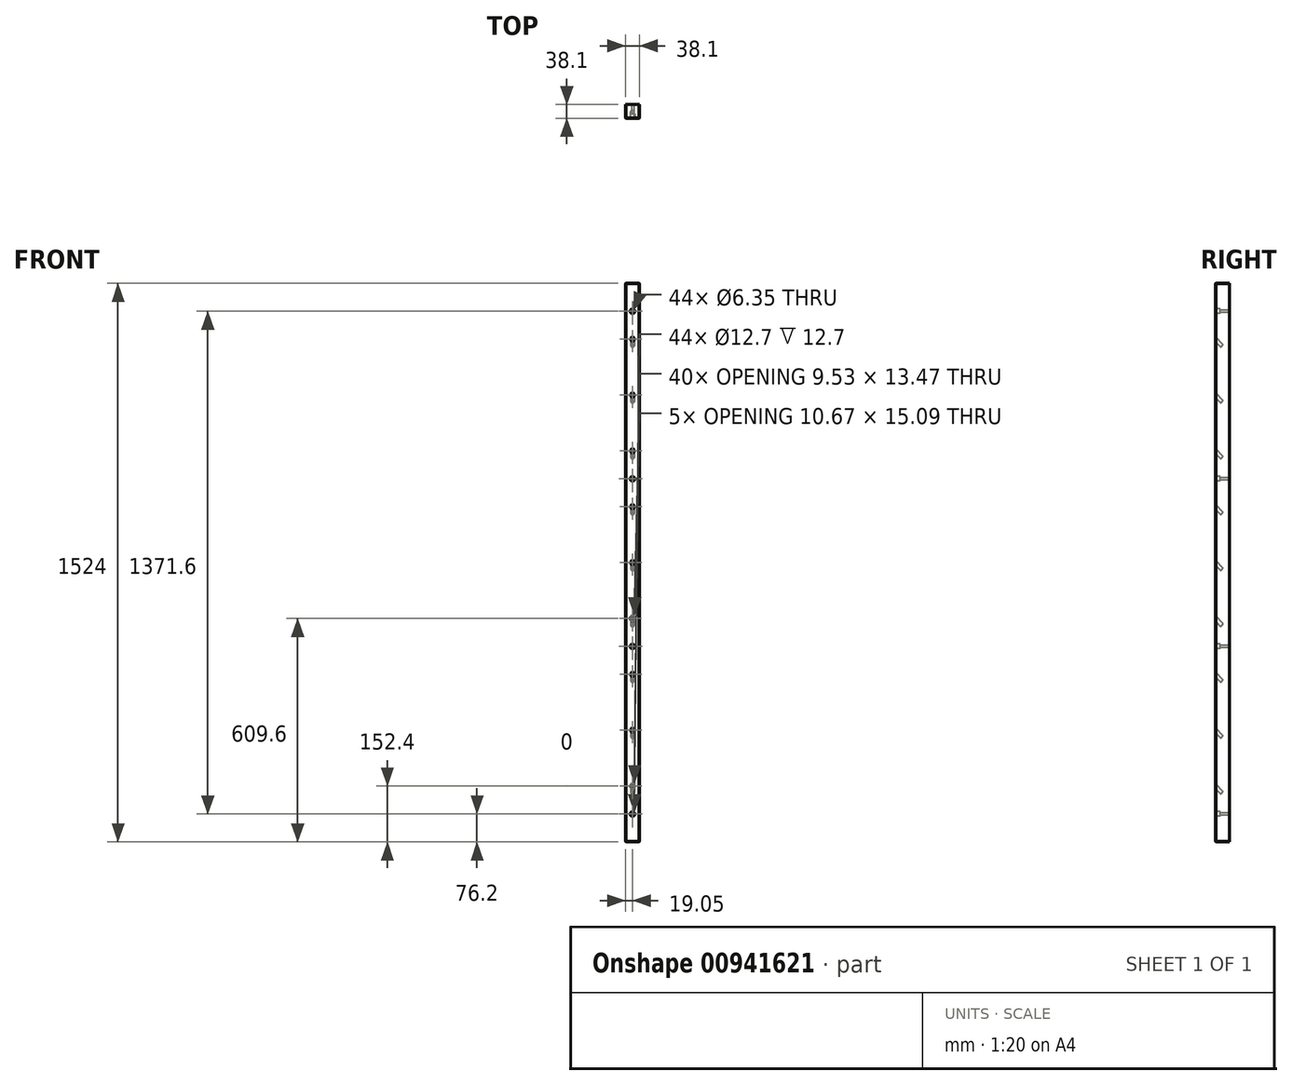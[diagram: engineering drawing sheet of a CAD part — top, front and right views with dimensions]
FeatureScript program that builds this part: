
annotation { "Feature Type Name" : "Feature", "Feature Type Description" : "" }
export const myFeature = defineFeature(function(context is Context, id is Id, definition is map)
    precondition{}
    {
        {
            var Q0;
            Q0=qCreatedBy(makeId("Front.planeOp"),FACE);
            var sketch = newSketch(context, id + "F0", { "sketchPlane" : qUnion([Q0])});
            skLineSegment(sketch, "E0.bottom", {"start": v(19.05, -762) * mm, "end": v(-19.05, -762) * mm});
            skLineSegment(sketch, "E0.top", {"start": v(19.05, 762) * mm, "end": v(-19.05, 762) * mm});
            skLineSegment(sketch, "E0.left", {"start": v(19.05, -762) * mm, "end": v(19.05, 762) * mm});
            skLineSegment(sketch, "E0.right", {"start": v(-19.05, -762) * mm, "end": v(-19.05, 762) * mm});
            skPoint(sketch, "E0.middle", {"position": v(0, 0) * mm});
            skSolve(sketch);
        }
        {
            var Q0;
            Q0=makeQuery(id+"F0.imprint","IMPRINT",FACE,{"disambiguationData":[TD([[makeQuery(id+"F0.imprint","IMPRINT",EDGE,{"derivedFrom":sQuery(id+"F0.wireOp",EDGE,"E0.bottom")}),-1.0]])]});
            extrude(context, id + "F1", {"entities" : qUnion([Q0]), "depth" : 38.1 * mm, "offsetDistance" : 25.4 * mm});
        }
        {
            var Q0;
            Q0=makeQuery(id+"F1.opExtrude","CAP_FACE",FACE,{"disambiguationData":[OSD([sQuery(id+"F0.wireOp",EDGE,"E0.bottom"),sQuery(id+"F0.wireOp",EDGE,"E0.top"),sQuery(id+"F0.wireOp",EDGE,"E0.left"),sQuery(id+"F0.wireOp",EDGE,"E0.right")])],"isStart":false});
            var sketch = newSketch(context, id + "F2", { "sketchPlane" : qUnion([Q0])});
            skPoint(sketch, "E1", {"position": v(0, 609.6) * mm});
            skPoint(sketch, "E1.positionSnap0", {"position": v(0, 762) * mm});
            skPoint(sketch, "E2", {"position": v(0, 457.2) * mm});
            skPoint(sketch, "E3", {"position": v(0, 304.8) * mm});
            skPoint(sketch, "E4", {"position": v(0, 152.4) * mm});
            skPoint(sketch, "E5", {"position": v(0, 0) * mm});
            skPoint(sketch, "E6", {"position": v(0, -152.4) * mm});
            skPoint(sketch, "E7", {"position": v(0, -304.8) * mm});
            skPoint(sketch, "E8", {"position": v(0, -457.2) * mm});
            skPoint(sketch, "E9", {"position": v(0, -609.6) * mm});
            skLineSegment(sketch, "E10", {"start": v(-19.05, 609.6) * mm, "end": v(19.05, 609.6) * mm});
            skLineSegment(sketch, "E11", {"start": v(-19.05, 457.2) * mm, "end": v(19.05, 457.2) * mm});
            skLineSegment(sketch, "E12", {"start": v(-19.05, 304.8) * mm, "end": v(19.05, 304.8) * mm});
            skLineSegment(sketch, "E13", {"start": v(-19.05, 152.4) * mm, "end": v(19.05, 152.4) * mm});
            skLineSegment(sketch, "E14", {"start": v(-19.05, -152.4) * mm, "end": v(19.05, -152.4) * mm});
            skLineSegment(sketch, "E15", {"start": v(-19.05, -304.8) * mm, "end": v(19.05, -304.8) * mm});
            skLineSegment(sketch, "E16", {"start": v(-19.05, -457.2) * mm, "end": v(19.05, -457.2) * mm});
            skLineSegment(sketch, "E17", {"start": v(-19.05, -609.6) * mm, "end": v(19.05, -609.6) * mm});
            skLineSegment(sketch, "E18", {"start": v(-19.05, 0) * mm, "end": v(19.05, 0) * mm});
            skPoint(sketch, "E19", {"position": v(0, 685.8) * mm});
            skPoint(sketch, "E20", {"position": v(0, 228.6) * mm});
            skPoint(sketch, "E21", {"position": v(0, -228.6) * mm});
            skPoint(sketch, "E22", {"position": v(0, -685.8) * mm});
            skSolve(sketch);
        }
        {
            var Q0;
            Q0=sQuery(id+"F2.wireOp",EDGE,"E10");
            cPlane(context, id + "F3", {"entities" : qUnion([Q0]), "cplaneType" : CPlaneType.LINE_ANGLE, "offset" : 25.4 * mm, "angle" : 135 * degree, "width" : 152.4 * mm, "height" : 152.4 * mm});
        }
        {
            var Q0;
            Q0=qCreatedBy(id+"F3.planeOp",FACE);
            var sketch = newSketch(context, id + "F4", { "sketchPlane" : qUnion([Q0])});
            skCircle(sketch, "E23", {"center": v(0, 404.11) * mm, "radius": 4.76 * mm});
            skSolve(sketch);
        }
        {
            var Q0;
            Q0=sQuery(id+"F2.wireOp",EDGE,"E11");
            cPlane(context, id + "F5", {"entities" : qUnion([Q0]), "cplaneType" : CPlaneType.LINE_ANGLE, "offset" : 25.4 * mm, "angle" : 135 * degree, "width" : 152.4 * mm, "height" : 152.4 * mm});
        }
        {
            var Q0;
            Q0=qCreatedBy(id+"F5.planeOp",FACE);
            var sketch = newSketch(context, id + "F6", { "sketchPlane" : qUnion([Q0])});
            skCircle(sketch, "E24", {"center": v(0, 296.35) * mm, "radius": 4.76 * mm});
            skSolve(sketch);
        }
        {
            var Q0;
            Q0=sQuery(id+"F2.wireOp",EDGE,"E12");
            cPlane(context, id + "F7", {"entities" : qUnion([Q0]), "cplaneType" : CPlaneType.LINE_ANGLE, "offset" : 25.4 * mm, "angle" : 135 * degree, "width" : 152.4 * mm, "height" : 152.4 * mm});
        }
        {
            var Q0;
            Q0=qCreatedBy(id+"F7.planeOp",FACE);
            var sketch = newSketch(context, id + "F8", { "sketchPlane" : qUnion([Q0])});
            skCircle(sketch, "E25", {"center": v(0, 188.59) * mm, "radius": 4.76 * mm});
            skSolve(sketch);
        }
        {
            var Q0;
            Q0=sQuery(id+"F2.wireOp",EDGE,"E13");
            cPlane(context, id + "F9", {"entities" : qUnion([Q0]), "cplaneType" : CPlaneType.LINE_ANGLE, "offset" : 25.4 * mm, "angle" : 135 * degree, "width" : 152.4 * mm, "height" : 152.4 * mm});
        }
        {
            var Q0;
            Q0=qCreatedBy(id+"F9.planeOp",FACE);
            var sketch = newSketch(context, id + "F10", { "sketchPlane" : qUnion([Q0])});
            skCircle(sketch, "E26", {"center": v(0, 80.82) * mm, "radius": 4.76 * mm});
            skSolve(sketch);
        }
        {
            var Q0;
            Q0=sQuery(id+"F2.wireOp",EDGE,"E18");
            cPlane(context, id + "F11", {"entities" : qUnion([Q0]), "cplaneType" : CPlaneType.LINE_ANGLE, "offset" : 25.4 * mm, "angle" : 135 * degree, "width" : 152.4 * mm, "height" : 152.4 * mm});
        }
        {
            var Q0;
            Q0=qCreatedBy(id+"F11.planeOp",FACE);
            var sketch = newSketch(context, id + "F12", { "sketchPlane" : qUnion([Q0])});
            skCircle(sketch, "E27", {"center": v(0, -26.94) * mm, "radius": 4.76 * mm});
            skSolve(sketch);
        }
        {
            var Q0;
            Q0=sQuery(id+"F2.wireOp",EDGE,"E14");
            cPlane(context, id + "F13", {"entities" : qUnion([Q0]), "cplaneType" : CPlaneType.LINE_ANGLE, "offset" : 25.4 * mm, "angle" : 135 * degree, "width" : 152.4 * mm, "height" : 152.4 * mm});
        }
        {
            var Q0;
            Q0=qCreatedBy(id+"F13.planeOp",FACE);
            var sketch = newSketch(context, id + "F14", { "sketchPlane" : qUnion([Q0])});
            skCircle(sketch, "E28", {"center": v(0, -134.7) * mm, "radius": 5.34 * mm});
            skSolve(sketch);
        }
        {
            var Q0;
            Q0=sQuery(id+"F2.wireOp",EDGE,"E15");
            cPlane(context, id + "F15", {"entities" : qUnion([Q0]), "cplaneType" : CPlaneType.LINE_ANGLE, "offset" : 25.4 * mm, "angle" : 135 * degree, "width" : 152.4 * mm, "height" : 152.4 * mm});
        }
        {
            var Q0;
            Q0=qCreatedBy(id+"F15.planeOp",FACE);
            var sketch = newSketch(context, id + "F16", { "sketchPlane" : qUnion([Q0])});
            skCircle(sketch, "E29", {"center": v(0, -242.47) * mm, "radius": 4.76 * mm});
            skSolve(sketch);
        }
        {
            var Q0;
            Q0=sQuery(id+"F2.wireOp",EDGE,"E16");
            cPlane(context, id + "F17", {"entities" : qUnion([Q0]), "cplaneType" : CPlaneType.LINE_ANGLE, "offset" : 25.4 * mm, "angle" : 135 * degree, "width" : 152.4 * mm, "height" : 152.4 * mm});
        }
        {
            var Q0;
            Q0=qCreatedBy(id+"F17.planeOp",FACE);
            var sketch = newSketch(context, id + "F18", { "sketchPlane" : qUnion([Q0])});
            skCircle(sketch, "E30", {"center": v(0, -350.23) * mm, "radius": 4.76 * mm});
            skSolve(sketch);
        }
        {
            var Q0;
            Q0=sQuery(id+"F2.wireOp",EDGE,"E17");
            cPlane(context, id + "F19", {"entities" : qUnion([Q0]), "cplaneType" : CPlaneType.LINE_ANGLE, "offset" : 25.4 * mm, "angle" : 135 * degree, "width" : 152.4 * mm, "height" : 152.4 * mm});
        }
        {
            var Q0;
            Q0=qCreatedBy(id+"F19.planeOp",FACE);
            var sketch = newSketch(context, id + "F20", { "sketchPlane" : qUnion([Q0])});
            skCircle(sketch, "E31", {"center": v(0, -458) * mm, "radius": 4.76 * mm});
            skSolve(sketch);
        }
        {
            var Q0;
            Q0=makeQuery(id+"F4.imprint","IMPRINT",FACE,{"disambiguationData":[TD([[makeQuery(id+"F4.imprint","IMPRINT",EDGE,{"derivedFrom":sQuery(id+"F4.wireOp",EDGE,"E23")}),1.0]])]});
            var Q1;
            Q1=makeQuery(id+"F6.imprint","IMPRINT",FACE,{"disambiguationData":[TD([[makeQuery(id+"F6.imprint","IMPRINT",EDGE,{"derivedFrom":sQuery(id+"F6.wireOp",EDGE,"E24")}),1.0]])]});
            var Q2;
            Q2=makeQuery(id+"F8.imprint","IMPRINT",FACE,{"disambiguationData":[TD([[makeQuery(id+"F8.imprint","IMPRINT",EDGE,{"derivedFrom":sQuery(id+"F8.wireOp",EDGE,"E25")}),1.0]])]});
            var Q3;
            Q3=makeQuery(id+"F10.imprint","IMPRINT",FACE,{"disambiguationData":[TD([[makeQuery(id+"F10.imprint","IMPRINT",EDGE,{"derivedFrom":sQuery(id+"F10.wireOp",EDGE,"E26")}),1.0]])]});
            var Q4;
            Q4=makeQuery(id+"F12.imprint","IMPRINT",FACE,{"disambiguationData":[TD([[makeQuery(id+"F12.imprint","IMPRINT",EDGE,{"derivedFrom":sQuery(id+"F12.wireOp",EDGE,"E27")}),1.0]])]});
            var Q5;
            Q5=makeQuery(id+"F14.imprint","IMPRINT",FACE,{"disambiguationData":[TD([[makeQuery(id+"F14.imprint","IMPRINT",EDGE,{"derivedFrom":sQuery(id+"F14.wireOp",EDGE,"E28")}),1.0]])]});
            var Q6;
            Q6=makeQuery(id+"F16.imprint","IMPRINT",FACE,{"disambiguationData":[TD([[makeQuery(id+"F16.imprint","IMPRINT",EDGE,{"derivedFrom":sQuery(id+"F16.wireOp",EDGE,"E29")}),1.0]])]});
            var Q7;
            Q7=makeQuery(id+"F18.imprint","IMPRINT",FACE,{"disambiguationData":[TD([[makeQuery(id+"F18.imprint","IMPRINT",EDGE,{"derivedFrom":sQuery(id+"F18.wireOp",EDGE,"E30")}),1.0]])]});
            var Q8;
            Q8=makeQuery(id+"F20.imprint","IMPRINT",FACE,{"disambiguationData":[TD([[makeQuery(id+"F20.imprint","IMPRINT",EDGE,{"derivedFrom":sQuery(id+"F20.wireOp",EDGE,"E31")}),1.0]])]});
            extrude(context, id + "F21", {"entities" : qUnion([Q0, Q1, Q2, Q3, Q4, Q5, Q6, Q7, Q8]), "operationType" : NewBodyOperationType.REMOVE, "endBound" : BoundingType.SYMMETRIC, "depth" : 50.8 * mm, "offsetDistance" : 25.4 * mm});
        }
        {
            var Q0;
            Q0=makeQuery(id+"F1.opExtrude","SWEPT_EDGE",EDGE,{"disambiguationData":[OSD([sQuery(id+"F0.wireOp",EDGE,"E0.top"),sQuery(id+"F0.wireOp",EDGE,"E0.left")])]});
            var Q1;
            Q1=makeQuery(id+"F1.opExtrude","CAP_EDGE",EDGE,{"disambiguationData":[OSD([sQuery(id+"F0.wireOp",EDGE,"E0.top")])],"isStart":false});
            var Q2;
            Q2=makeQuery(id+"F1.opExtrude","SWEPT_EDGE",EDGE,{"disambiguationData":[OSD([sQuery(id+"F0.wireOp",EDGE,"E0.top"),sQuery(id+"F0.wireOp",EDGE,"E0.right")])]});
            var Q3;
            Q3=makeQuery(id+"F1.opExtrude","CAP_EDGE",EDGE,{"disambiguationData":[OSD([sQuery(id+"F0.wireOp",EDGE,"E0.left")])],"isStart":false});
            var Q4;
            Q4=makeQuery(id+"F1.opExtrude","CAP_EDGE",EDGE,{"disambiguationData":[OSD([sQuery(id+"F0.wireOp",EDGE,"E0.right")])],"isStart":false});
            var Q5;
            Q5=makeQuery(id+"F1.opExtrude","CAP_EDGE",EDGE,{"disambiguationData":[OSD([sQuery(id+"F0.wireOp",EDGE,"E0.bottom")])],"isStart":false});
            var Q6;
            Q6=makeQuery(id+"F1.opExtrude","SWEPT_EDGE",EDGE,{"disambiguationData":[OSD([sQuery(id+"F0.wireOp",EDGE,"E0.bottom"),sQuery(id+"F0.wireOp",EDGE,"E0.left")])]});
            var Q7;
            Q7=makeQuery(id+"F1.opExtrude","SWEPT_EDGE",EDGE,{"disambiguationData":[OSD([sQuery(id+"F0.wireOp",EDGE,"E0.bottom"),sQuery(id+"F0.wireOp",EDGE,"E0.right")])]});
            chamfer(context, id + "F22", {"entities" : qUnion([Q0, Q1, Q2, Q3, Q4, Q5, Q6, Q7]), "width" : 1.27 * mm, "tangentPropagation" : true});
        }
        {
            var Q0;
            Q0=sQuery(id+"F2.wireOp",VERTEX,"E19");
            var Q1;
            Q1=sQuery(id+"F2.wireOp",VERTEX,"E20");
            var Q2;
            Q2=sQuery(id+"F2.wireOp",VERTEX,"E21");
            var Q3;
            Q3=sQuery(id+"F2.wireOp",VERTEX,"E22");
            var Q4;
            Q4=makeQuery(id+"F1.opExtrude","SWEPT_BODY",BODY,{"disambiguationData":[OSD([sQuery(id+"F0.wireOp",EDGE,"E0.bottom"),sQuery(id+"F0.wireOp",EDGE,"E0.top"),sQuery(id+"F0.wireOp",EDGE,"E0.left"),sQuery(id+"F0.wireOp",EDGE,"E0.right")])]});
            hole(context, id + "F23", {"style" : HoleStyle.C_BORE, "endStyle" : HoleEndStyle.THROUGH, "holeDiameter" : 6.35 * mm, "cBoreDiameter" : 12.7 * mm, "cBoreDepth" : 12.7 * mm, "majorDiameter" : 6.35 * mm, "isTappedThrough" : true, "tappedDepth" : 12.7 * mm, "tapClearance" : 3, "locations" : qUnion([Q0, Q1, Q2, Q3]), "scope" : qUnion([Q4])});
        }
    });
